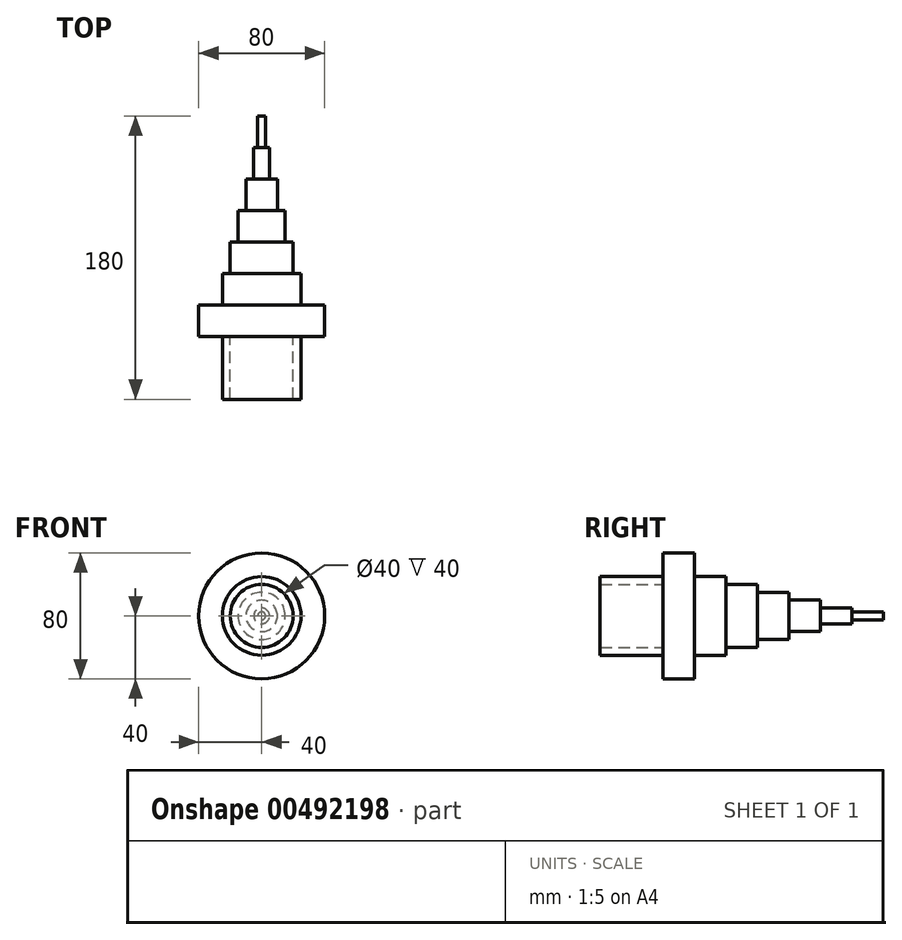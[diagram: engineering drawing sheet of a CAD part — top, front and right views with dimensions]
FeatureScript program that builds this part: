
annotation { "Feature Type Name" : "Feature", "Feature Type Description" : "" }
export const myFeature = defineFeature(function(context is Context, id is Id, definition is map)
    precondition{}
    {
        {
            var Q0;
            Q0=qCreatedBy(makeId("Front.planeOp"),FACE);
            var sketch = newSketch(context, id + "F0", { "sketchPlane" : qUnion([Q0])});
            skCircle(sketch, "E0", {"center": v(0, 0) * mm, "radius": 40 * mm});
            skSolve(sketch);
        }
        {
            var Q0;
            Q0=makeQuery(id+"F0.imprint","IMPRINT",FACE,{"disambiguationData":[TD([[makeQuery(id+"F0.imprint","IMPRINT",EDGE,{"derivedFrom":sQuery(id+"F0.wireOp",EDGE,"E0")}),1.0]])]});
            extrude(context, id + "F1", {"entities" : qUnion([Q0]), "endBound" : BoundingType.SYMMETRIC, "depth" : (180 - (20 * 8)) * mm, "offsetDistance" : 25 * mm});
        }
        {
            var Q0;
            Q0=makeQuery(id+"F1.opExtrude","CAP_FACE",FACE,{"disambiguationData":[OSD([sQuery(id+"F0.wireOp",EDGE,"E0")])],"isStart":true});
            var sketch = newSketch(context, id + "F2", { "sketchPlane" : qUnion([Q0])});
            skCircle(sketch, "E1", {"center": v(0, 0) * mm, "radius": 25 * mm});
            skSolve(sketch);
        }
        {
            var Q0;
            Q0 = qSketchRegion(id + "F2", true);
            extrude(context, id + "F3", {"entities" : qUnion([Q0]), "operationType" : NewBodyOperationType.ADD, "depth" : 20 * mm, "offsetDistance" : 25 * mm});
        }
        {
            var Q0;
            Q0=makeQuery(id+"F3.opExtrude","CAP_FACE",FACE,{"disambiguationData":[OSD([sQuery(id+"F2.wireOp",EDGE,"E1")])],"isStart":false});
            var sketch = newSketch(context, id + "F4", { "sketchPlane" : qUnion([Q0])});
            skCircle(sketch, "E2", {"center": v(0, 0) * mm, "radius": 20 * mm});
            skSolve(sketch);
        }
        {
            var Q0;
            Q0=makeQuery(id+"F4.imprint","IMPRINT",FACE,{"disambiguationData":[TD([[makeQuery(id+"F4.imprint","IMPRINT",EDGE,{"derivedFrom":sQuery(id+"F4.wireOp",EDGE,"E2")}),1.0]])]});
            var Q1;
            Q1=sQuery(id+"F4.wireOp",EDGE,"E2");
            extrude(context, id + "F5", {"entities" : qUnion([Q0]), "operationType" : NewBodyOperationType.ADD, "surfaceEntities" : qUnion([Q1]), "depth" : 20 * mm, "offsetDistance" : 25 * mm});
        }
        {
            var Q0;
            Q0=makeQuery(id+"F5.opExtrude","CAP_FACE",FACE,{"disambiguationData":[OSD([sQuery(id+"F4.wireOp",EDGE,"E2")])],"isStart":false});
            var sketch = newSketch(context, id + "F6", { "sketchPlane" : qUnion([Q0])});
            skCircle(sketch, "E3", {"center": v(0, 0) * mm, "radius": 15 * mm});
            skSolve(sketch);
        }
        {
            var Q0;
            Q0 = qSketchRegion(id + "F6", true);
            extrude(context, id + "F7", {"entities" : qUnion([Q0]), "operationType" : NewBodyOperationType.ADD, "depth" : 20 * mm, "offsetDistance" : 25 * mm});
        }
        {
            var Q0;
            Q0=makeQuery(id+"F7.opExtrude","CAP_FACE",FACE,{"disambiguationData":[OSD([sQuery(id+"F6.wireOp",EDGE,"E3")])],"isStart":false});
            var sketch = newSketch(context, id + "F8", { "sketchPlane" : qUnion([Q0])});
            skCircle(sketch, "E4", {"center": v(0, 0) * mm, "radius": 10 * mm});
            skSolve(sketch);
        }
        {
            var Q0;
            Q0 = qSketchRegion(id + "F8", true);
            extrude(context, id + "F9", {"entities" : qUnion([Q0]), "operationType" : NewBodyOperationType.ADD, "depth" : 20 * mm, "offsetDistance" : 25 * mm});
        }
        {
            var Q0;
            Q0=makeQuery(id+"F9.opExtrude","CAP_FACE",FACE,{"disambiguationData":[OSD([sQuery(id+"F8.wireOp",EDGE,"E4")])],"isStart":false});
            var sketch = newSketch(context, id + "F10", { "sketchPlane" : qUnion([Q0])});
            skCircle(sketch, "E5", {"center": v(0, 0) * mm, "radius": 5 * mm});
            skSolve(sketch);
        }
        {
            var Q0;
            Q0 = qSketchRegion(id + "F10", true);
            extrude(context, id + "F11", {"entities" : qUnion([Q0]), "operationType" : NewBodyOperationType.ADD, "depth" : 20 * mm, "offsetDistance" : 25 * mm});
        }
        {
            var Q0;
            Q0=makeQuery(id+"F11.opExtrude","CAP_FACE",FACE,{"disambiguationData":[OSD([sQuery(id+"F10.wireOp",EDGE,"E5")])],"isStart":false});
            var sketch = newSketch(context, id + "F12", { "sketchPlane" : qUnion([Q0])});
            skCircle(sketch, "E6", {"center": v(0, 0) * mm, "radius": 2.5 * mm});
            skSolve(sketch);
        }
        {
            var Q0;
            Q0 = qSketchRegion(id + "F12", true);
            extrude(context, id + "F13", {"entities" : qUnion([Q0]), "operationType" : NewBodyOperationType.ADD, "depth" : 20 * mm, "offsetDistance" : 25 * mm});
        }
        {
            var Q0;
            Q0=makeQuery(id+"F1.opExtrude","CAP_FACE",FACE,{"disambiguationData":[OSD([sQuery(id+"F0.wireOp",EDGE,"E0")])],"isStart":false});
            var sketch = newSketch(context, id + "F14", { "sketchPlane" : qUnion([Q0])});
            skCircle(sketch, "E7", {"center": v(0, 0) * mm, "radius": 25 * mm});
            skCircle(sketch, "E8", {"center": v(0, 0) * mm, "radius": 20 * mm});
            skSolve(sketch);
        }
        {
            var Q0;
            Q0 = qSketchRegion(id + "F14", true);
            extrude(context, id + "F15", {"entities" : qUnion([Q0]), "operationType" : NewBodyOperationType.ADD, "depth" : 40 * mm, "offsetDistance" : 25 * mm});
        }
    });
